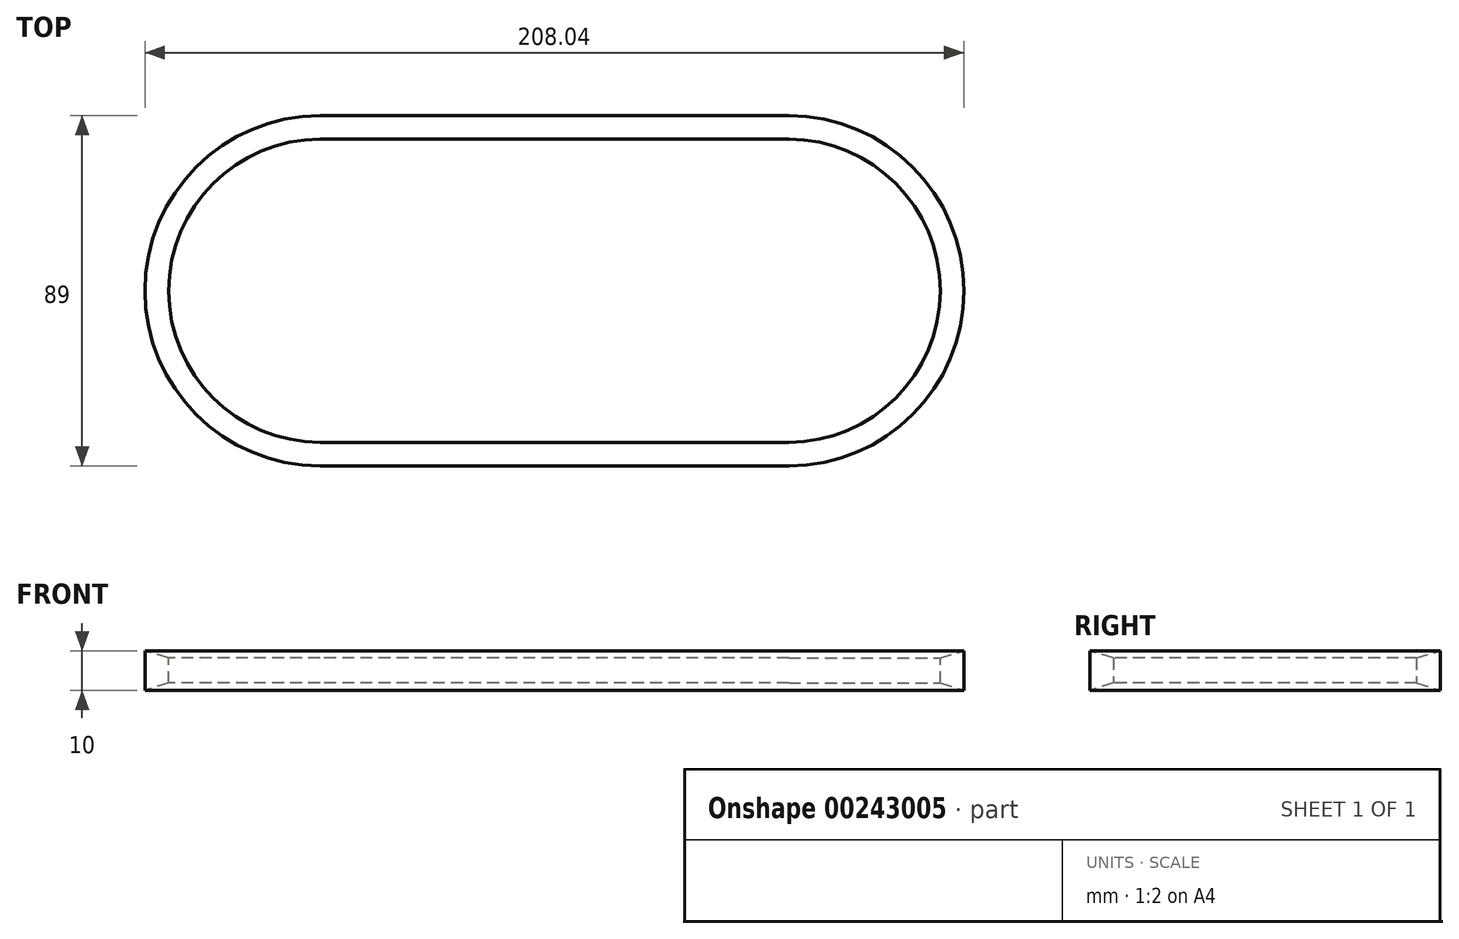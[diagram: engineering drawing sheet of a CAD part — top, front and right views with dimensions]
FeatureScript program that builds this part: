
annotation { "Feature Type Name" : "Feature", "Feature Type Description" : "" }
export const myFeature = defineFeature(function(context is Context, id is Id, definition is map)
    precondition{}
    {
        {
            var Q0;
            Q0=qCreatedBy(makeId("Top.planeOp"),FACE);
            var sketch = newSketch(context, id + "F0", { "sketchPlane" : qUnion([Q0])});
            skLineSegment(sketch, "E0", {"start": v(0, 0) * mm, "end": v(-59.52, 0) * mm});
            skLineSegment(sketch, "E1", {"start": v(-59.52, 77) * mm, "end": v(0, 77) * mm});
            skArc(sketch, "E2", {"start": v(-59.52, 77) * mm, "mid": v(-98.02, 38.5) * mm, "end": v(-59.52, 0) * mm});
            skLineSegment(sketch, "E3.MirrorCS", {"start": v(59.52, 77) * mm, "end": v(0, 77) * mm});
            skArc(sketch, "E4.MirrorCS", {"start": v(59.52, 77) * mm, "mid": v(98.02, 38.5) * mm, "end": v(59.52, 0) * mm});
            skLineSegment(sketch, "E5.MirrorCS", {"start": v(0, 0) * mm, "end": v(59.52, 0) * mm});
            skSolve(sketch);
        }
        {
            var Q0;
            Q0=qCreatedBy(makeId("Right.planeOp"),FACE);
            var sketch = newSketch(context, id + "F1", { "sketchPlane" : qUnion([Q0])});
            skLineSegment(sketch, "E6", {"start": v(0, 0) * mm, "end": v(0, 3.17) * mm});
            skLineSegment(sketch, "E7", {"start": v(0, 3.17) * mm, "end": v(-6, 5) * mm});
            skLineSegment(sketch, "E8", {"start": v(-6, 5) * mm, "end": v(-6, 0) * mm});
            skLineSegment(sketch, "E9.MirrorCS", {"start": v(0, -3.17) * mm, "end": v(-6, -5) * mm});
            skLineSegment(sketch, "E10.MirrorCS", {"start": v(0, 0) * mm, "end": v(0, -3.17) * mm});
            skLineSegment(sketch, "E11.MirrorCS", {"start": v(-6, -5) * mm, "end": v(-6, 0) * mm});
            skSolve(sketch);
        }
        {
            var Q0;
            Q0=makeQuery(id+"F1.imprint","IMPRINT",FACE,{"disambiguationData":[TD([[makeQuery(id+"F1.imprint","IMPRINT",EDGE,{"derivedFrom":sQuery(id+"F1.wireOp",EDGE,"E6")}),1.0]])]});
            var Q1;
            Q1=sQuery(id+"F0.wireOp",EDGE,"E0");
            var Q2;
            Q2=sQuery(id+"F0.wireOp",EDGE,"E2");
            var Q3;
            Q3=sQuery(id+"F0.wireOp",EDGE,"E1");
            var Q4;
            Q4=sQuery(id+"F0.wireOp",EDGE,"E3.MirrorCS");
            var Q5;
            Q5=sQuery(id+"F0.wireOp",EDGE,"E4.MirrorCS");
            var Q6;
            Q6=sQuery(id+"F0.wireOp",EDGE,"E5.MirrorCS");
            sweep(context, id + "F2", {"profiles" : qUnion([Q0]), "path" : qUnion([Q1, Q2, Q3, Q4, Q5, Q6])});
        }
    });
